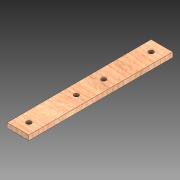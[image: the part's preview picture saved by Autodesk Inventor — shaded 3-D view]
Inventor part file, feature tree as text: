
AUTODESK INVENTOR PART (.ipt)
format: ipt  version: 2020 (Build 240168000, 168)  size: 111,616 bytes
history: native  units: mm
features: extrude x1, sketch x1
ambient origin geometry x8: Origin, YZ Plane, XZ Plane, XY Plane, X Axis, Y Axis, Z Axis, Center Point
bodies: Solid1 (feature_tree)
feature tree (2):
  extrude  "Extrusion1"  Depth=45.0mm
  sketch  "Sketch1"  dims[d0=300.0mm d1=45.0mm d2=10.0mm d3=10.0mm d4=22.5mm d5=22.5mm d6=22.5mm d7=22.5mm d8=150.0mm d9=9.6mm d10=28.5mm d11=22.5mm d12=22.5mm d13=28.5mm d14=10.0mm d15=0.0mm]
